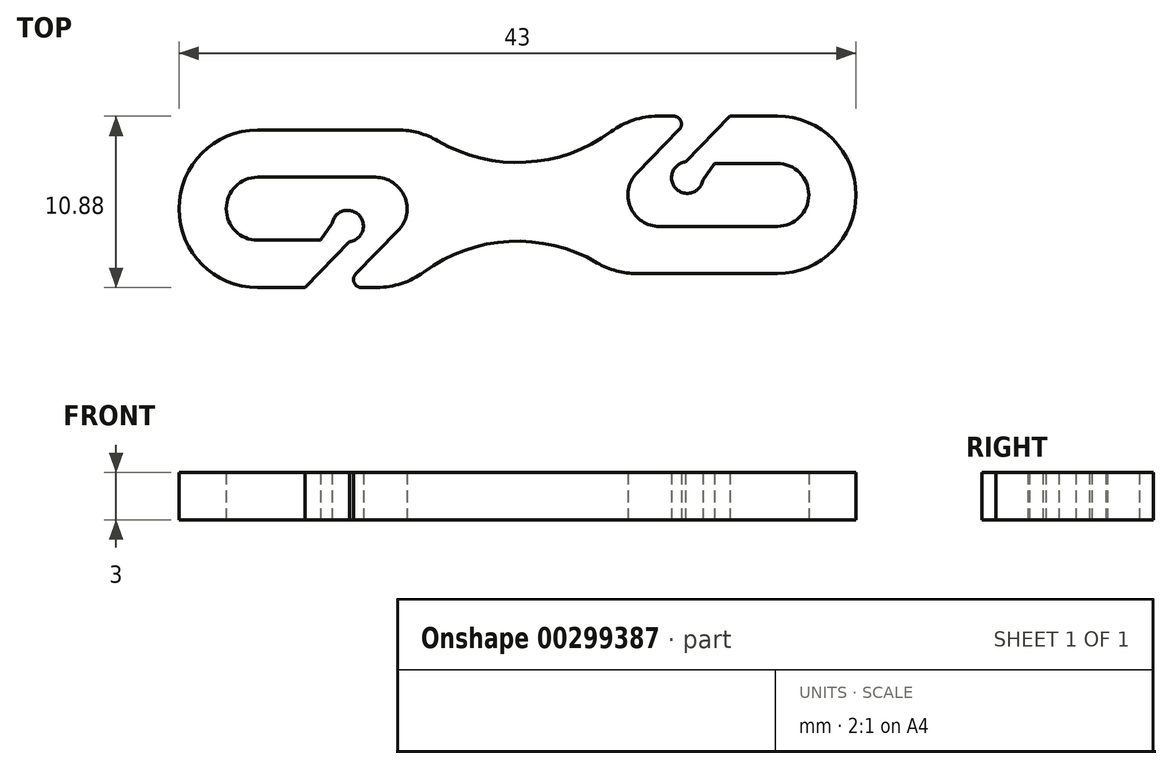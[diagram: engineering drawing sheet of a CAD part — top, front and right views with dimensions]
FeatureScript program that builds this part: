
annotation { "Feature Type Name" : "Feature", "Feature Type Description" : "" }
export const myFeature = defineFeature(function(context is Context, id is Id, definition is map)
    precondition{}
    {
        {
            var Q0;
            Q0=qCreatedBy(makeId("Top.planeOp"),FACE);
            var sketch = newSketch(context, id + "F0", { "sketchPlane" : qUnion([Q0])});
            skArc(sketch, "E0", {"start": v(-16.5, 5) * mm, "mid": v(-21.5, 0) * mm, "end": v(-16.5, -5) * mm});
            skPoint(sketch, "E0.centerSnap0", {"position": v(-21.5, 0) * mm});
            skLineSegment(sketch, "E1.trimOffspring", {"start": v(-7.59, 5) * mm, "end": v(-16.5, 5) * mm});
            skArc(sketch, "E2.0", {"start": v(-16.5, 2) * mm, "mid": v(-18.5, 0) * mm, "end": v(-16.5, -2) * mm});
            skLineSegment(sketch, "E3.0", {"start": v(-9.02, 2) * mm, "end": v(-16.5, 2) * mm});
            skLineSegment(sketch, "E4.trimOffspring", {"start": v(-13.5, -5) * mm, "end": v(-16.5, -5) * mm});
            skArc(sketch, "E5", {"start": v(-10.66, -2.1) * mm, "mid": v(-10.07, -0.4) * mm, "end": v(-11.77, -0.94) * mm});
            skLineSegment(sketch, "E6", {"start": v(-13.5, -5) * mm, "end": v(-10.66, -2.1) * mm});
            skLineSegment(sketch, "E7", {"start": v(-12.5, -2) * mm, "end": v(-11.77, -0.94) * mm});
            skLineSegment(sketch, "E8.trimOffspring", {"start": v(-12.5, -2) * mm, "end": v(-16.5, -2) * mm});
            skLineSegment(sketch, "E9", {"start": v(-9.91, -5) * mm, "end": v(-8.92, -5) * mm});
            skLineSegment(sketch, "E10", {"start": v(-7.58, -1.4) * mm, "end": v(-10.27, -4.15) * mm});
            skArc(sketch, "E11.filletArc", {"start": v(-10.27, -4.15) * mm, "mid": v(-10.37, -4.7) * mm, "end": v(-9.91, -5) * mm});
            skArc(sketch, "E12.filletArc", {"start": v(-7.58, -1.4) * mm, "mid": v(-7.17, 0.78) * mm, "end": v(-9.02, 2) * mm});
            skArc(sketch, "E13", {"start": v(-5.06, 4.31) * mm, "mid": v(-2.62, 3.29) * mm, "end": v(0, 2.94) * mm});
            skArc(sketch, "E14.filletArc", {"start": v(-5.06, 4.31) * mm, "mid": v(-6.28, 4.83) * mm, "end": v(-7.59, 5) * mm});
            skArc(sketch, "E15", {"start": v(0, -2.06) * mm, "mid": v(-3.13, -2.56) * mm, "end": v(-5.95, -4.02) * mm});
            skArc(sketch, "E16.filletArc", {"start": v(-8.92, -5) * mm, "mid": v(-7.35, -4.75) * mm, "end": v(-5.95, -4.02) * mm});
            skPoint(sketch, "E17.1.0", {"position": v(21.5, 0.88) * mm});
            skLineSegment(sketch, "E17.1.1", {"start": v(7.59, -4.12) * mm, "end": v(16.5, -4.12) * mm});
            skArc(sketch, "E17.1.2", {"start": v(7.58, 2.28) * mm, "mid": v(7.17, 0.1) * mm, "end": v(9.02, -1.12) * mm});
            skLineSegment(sketch, "E17.1.3", {"start": v(13.5, 5.88) * mm, "end": v(10.66, 2.97) * mm});
            skArc(sketch, "E17.1.4", {"start": v(5.06, -3.43) * mm, "mid": v(2.62, -2.41) * mm, "end": v(0, -2.06) * mm});
            skLineSegment(sketch, "E17.1.5", {"start": v(12.5, 2.88) * mm, "end": v(16.5, 2.88) * mm});
            skArc(sketch, "E17.1.6", {"start": v(8.92, 5.88) * mm, "mid": v(7.35, 5.63) * mm, "end": v(5.95, 4.9) * mm});
            skArc(sketch, "E17.1.7", {"start": v(5.06, -3.43) * mm, "mid": v(6.28, -3.95) * mm, "end": v(7.59, -4.12) * mm});
            skArc(sketch, "E17.1.8", {"start": v(16.5, -4.12) * mm, "mid": v(21.5, 0.88) * mm, "end": v(16.5, 5.88) * mm});
            skLineSegment(sketch, "E17.1.9", {"start": v(9.02, -1.12) * mm, "end": v(16.5, -1.12) * mm});
            skLineSegment(sketch, "E17.1.10", {"start": v(13.5, 5.88) * mm, "end": v(16.5, 5.88) * mm});
            skArc(sketch, "E17.1.11", {"start": v(10.66, 2.97) * mm, "mid": v(10.07, 1.28) * mm, "end": v(11.77, 1.82) * mm});
            skLineSegment(sketch, "E17.1.12", {"start": v(7.58, 2.28) * mm, "end": v(10.27, 5.03) * mm});
            skArc(sketch, "E17.1.13", {"start": v(0, 2.94) * mm, "mid": v(3.13, 3.44) * mm, "end": v(5.95, 4.9) * mm});
            skArc(sketch, "E17.1.14", {"start": v(16.5, -1.12) * mm, "mid": v(18.5, 0.88) * mm, "end": v(16.5, 2.88) * mm});
            skLineSegment(sketch, "E17.1.15", {"start": v(9.91, 5.88) * mm, "end": v(8.92, 5.88) * mm});
            skLineSegment(sketch, "E17.1.16", {"start": v(12.5, 2.88) * mm, "end": v(11.77, 1.82) * mm});
            skArc(sketch, "E17.1.17", {"start": v(10.27, 5.03) * mm, "mid": v(10.37, 5.57) * mm, "end": v(9.91, 5.88) * mm});
            skSolve(sketch);
        }
        {
            var Q0;
            Q0=makeQuery(id+"F0.imprint","IMPRINT",FACE,{"disambiguationData":[TD([[makeQuery(id+"F0.imprint","IMPRINT",EDGE,{"derivedFrom":sQuery(id+"F0.wireOp",EDGE,"E0")}),1.0]])]});
            extrude(context, id + "F1", {"entities" : qUnion([Q0]), "depth" : 3 * mm});
        }
    });
